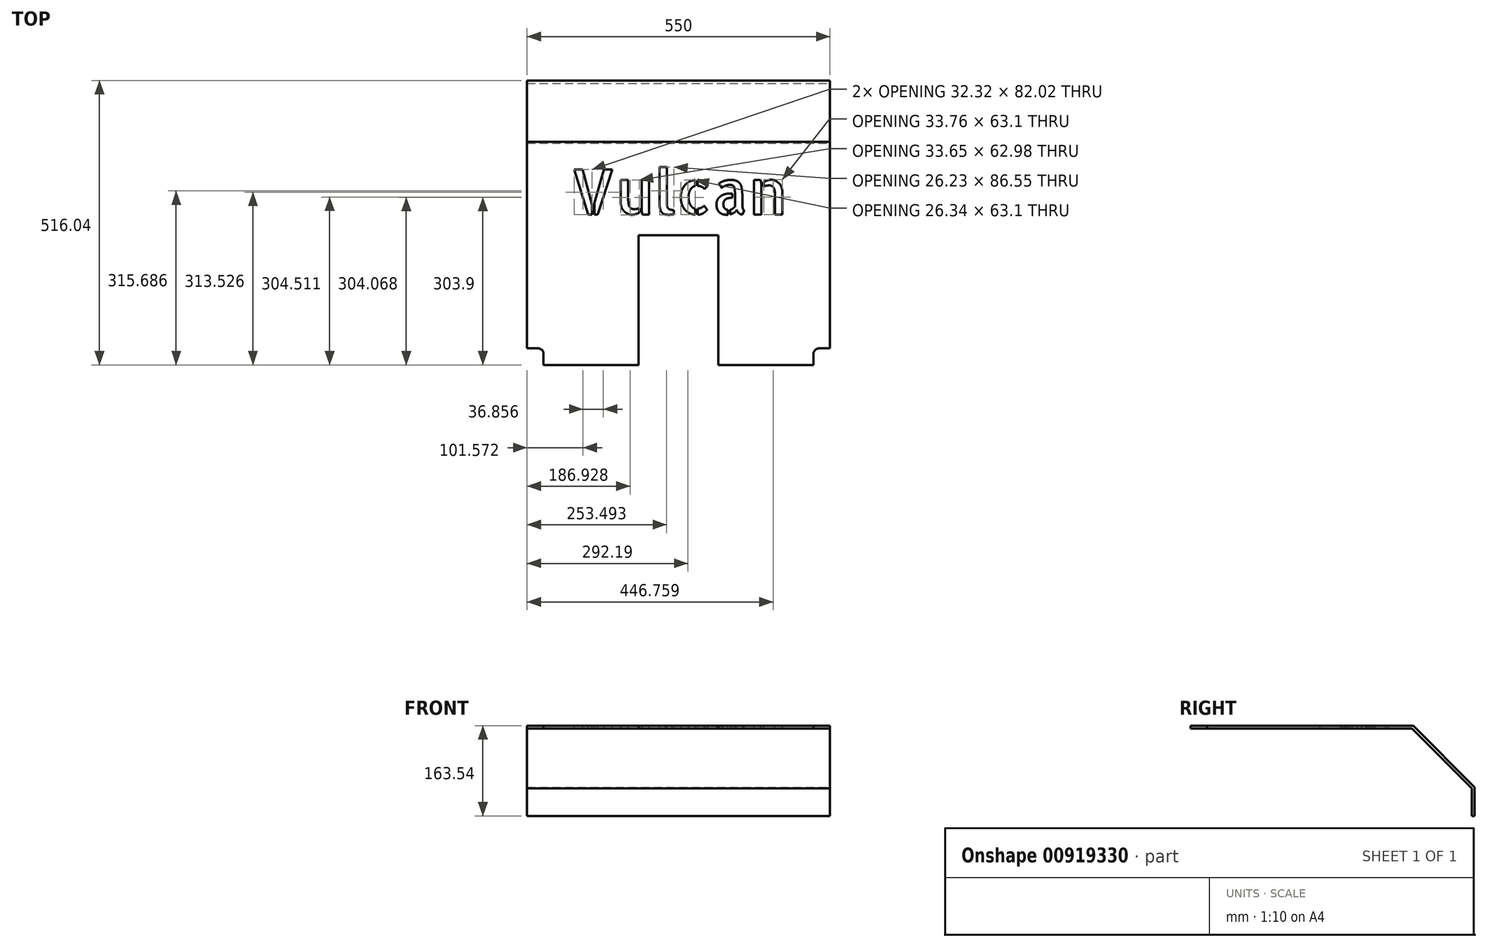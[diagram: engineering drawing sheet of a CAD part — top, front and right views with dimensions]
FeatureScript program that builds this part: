
annotation { "Feature Type Name" : "Feature", "Feature Type Description" : "" }
export const myFeature = defineFeature(function(context is Context, id is Id, definition is map)
    precondition{}
    {
        {
            var Q0;
            Q0=qCreatedBy(makeId("Front.planeOp"),FACE);
            var sketch = newSketch(context, id + "F0", { "sketchPlane" : qUnion([Q0])});
            skLineSegment(sketch, "E0.bottom", {"start": v(0, 0) * mm, "end": v(-550, 0) * mm});
            skLineSegment(sketch, "E0.top", {"start": v(0, 55) * mm, "end": v(-550, 55) * mm});
            skLineSegment(sketch, "E0.left", {"start": v(0, 0) * mm, "end": v(0, 55) * mm});
            skLineSegment(sketch, "E0.right", {"start": v(-550, 0) * mm, "end": v(-550, 55) * mm});
            skSolve(sketch);
        }
        {
            var Q0;
            Q0 = qSketchRegion(id + "F0", true);
            extrude(context, id + "F1", {"entities" : qUnion([Q0]), "depth" : 5 * mm, "offsetDistance" : 25 * mm});
        }
        {
            var Q0;
            Q0=makeQuery(id+"F1.opExtrude","SWEPT_FACE",FACE,{"disambiguationData":[OSD([sQuery(id+"F0.wireOp",EDGE,"E0.left")])]});
            var sketch = newSketch(context, id + "F2", { "sketchPlane" : qUnion([Q0])});
            skLineSegment(sketch, "E1", {"start": v(0, 55) * mm, "end": v(-5, 50) * mm});
            skSolve(sketch);
        }
        {
            var Q0;
            {var subQ0=sQuery(id+"F2.wireOp",EDGE,"E1");Q0=makeQuery(id+"F2.imprint","IMPRINT",FACE,{"disambiguationData":[TD([[makeQuery(id+"F2.imprint","IMPRINT",EDGE,{"derivedFrom":subQ0}),-1.0]])]});}
            extrude(context, id + "F3", {"entities" : qUnion([Q0]), "operationType" : NewBodyOperationType.REMOVE, "endBound" : BoundingType.THROUGH_ALL, "oppositeDirection" : true, "depth" : 25 * mm, "offsetDistance" : 25 * mm});
        }
        {
            var Q0;
            Q0=makeQuery(id+"F3.boolean.opBoolean","COPY",FACE,{"derivedFrom":makeQuery(id+"F3.opExtrude","SWEPT_FACE",FACE,{"disambiguationData":[OSD([sQuery(id+"F2.wireOp",EDGE,"E1")])]})});
            extrude(context, id + "F4", {"entities" : qUnion([Q0]), "operationType" : NewBodyOperationType.ADD, "depth" : 160.56 * mm, "offsetDistance" : 25 * mm});
        }
        {
            var Q0;
            Q0=makeQuery(id+"F4.boolean.opBoolean","MERGE",FACE,{"derivedFrom":[makeQuery(id+"F1.opExtrude","SWEPT_FACE",FACE,{"disambiguationData":[OSD([sQuery(id+"F0.wireOp",EDGE,"E0.left")])]}),makeQuery(id+"F4.opExtrude","SWEPT_FACE",FACE,{"disambiguationData":[OSD([sQuery(id+"F2.wireOp",EDGE,"E1")])]})]});
            var sketch = newSketch(context, id + "F5", { "sketchPlane" : qUnion([Q0])});
            skLineSegment(sketch, "E2", {"start": v(-113.54, 168.54) * mm, "end": v(-113.54, 158.54) * mm});
            skSolve(sketch);
        }
        {
            var Q0;
            {var subQ0=sQuery(id+"F5.wireOp",EDGE,"E2");Q0=makeQuery(id+"F5.imprint","IMPRINT",FACE,{"disambiguationData":[TD([[makeQuery(id+"F5.imprint","IMPRINT",EDGE,{"derivedFrom":subQ0}),-1.0]])]});}
            extrude(context, id + "F6", {"entities" : qUnion([Q0]), "operationType" : NewBodyOperationType.REMOVE, "endBound" : BoundingType.THROUGH_ALL, "oppositeDirection" : true, "depth" : 25 * mm, "offsetDistance" : 25 * mm});
        }
        {
            var Q0;
            Q0=makeQuery(id+"F6.boolean.opBoolean","COPY",FACE,{"derivedFrom":makeQuery(id+"F6.opExtrude","SWEPT_FACE",FACE,{"disambiguationData":[OSD([sQuery(id+"F5.wireOp",EDGE,"E2")])]})});
            extrude(context, id + "F7", {"entities" : qUnion([Q0]), "operationType" : NewBodyOperationType.ADD, "depth" : 402.5 * mm, "offsetDistance" : 25 * mm});
        }
        {
            var Q0;
            Q0=makeQuery(id+"F7.opExtrude","CAP_FACE",FACE,{"disambiguationData":[OSD([sQuery(id+"F5.wireOp",EDGE,"E2")])],"isStart":false});
            var sketch = newSketch(context, id + "F8", { "sketchPlane" : qUnion([Q0])});
            skLineSegment(sketch, "E3", {"start": v(-550, 163.54) * mm, "end": v(0, 163.54) * mm});
            skSolve(sketch);
        }
        {
            var Q0;
            {var subQ0=sQuery(id+"F8.wireOp",EDGE,"E3");Q0=makeQuery(id+"F8.imprint","IMPRINT",FACE,{"disambiguationData":[TD([[makeQuery(id+"F8.imprint","IMPRINT",EDGE,{"derivedFrom":subQ0}),1.0]])]});}
            extrude(context, id + "F9", {"entities" : qUnion([Q0]), "operationType" : NewBodyOperationType.REMOVE, "endBound" : BoundingType.THROUGH_ALL, "oppositeDirection" : true, "depth" : 25 * mm, "offsetDistance" : 25 * mm});
        }
        {
            var Q0;
            Q0=makeQuery(id+"F7.boolean.opBoolean","MERGE",FACE,{"derivedFrom":[makeQuery(id+"F4.boolean.opBoolean","MERGE",FACE,{"derivedFrom":[makeQuery(id+"F1.opExtrude","SWEPT_FACE",FACE,{"disambiguationData":[OSD([sQuery(id+"F0.wireOp",EDGE,"E0.left")])]}),makeQuery(id+"F4.opExtrude","SWEPT_FACE",FACE,{"disambiguationData":[OSD([sQuery(id+"F2.wireOp",EDGE,"E1")])]})]}),makeQuery(id+"F7.opExtrude","SWEPT_FACE",FACE,{"disambiguationData":[OSD([sQuery(id+"F5.wireOp",EDGE,"E2")])]})]});
            var sketch = newSketch(context, id + "F10", { "sketchPlane" : qUnion([Q0])});
            skLineSegment(sketch, "E4", {"start": v(-111.46, 163.54) * mm, "end": v(0, 52.07) * mm});
            skSolve(sketch);
        }
        {
            var Q0;
            {var subQ0=sQuery(id+"F10.wireOp",EDGE,"E4");Q0=makeQuery(id+"F10.imprint","IMPRINT",FACE,{"disambiguationData":[TD([[makeQuery(id+"F10.imprint","IMPRINT",EDGE,{"derivedFrom":subQ0}),1.0]])]});}
            extrude(context, id + "F11", {"entities" : qUnion([Q0]), "operationType" : NewBodyOperationType.REMOVE, "endBound" : BoundingType.THROUGH_ALL, "oppositeDirection" : true, "depth" : 25 * mm, "offsetDistance" : 25 * mm});
        }
        {
            var Q0;
            Q0=makeQuery(id+"F9.boolean.opBoolean","COPY",FACE,{"derivedFrom":makeQuery(id+"F9.opExtrude","SWEPT_FACE",FACE,{"disambiguationData":[OSD([sQuery(id+"F8.wireOp",EDGE,"E3")])]})});
            var sketch = newSketch(context, id + "F12", { "sketchPlane" : qUnion([Q0])});
            skLineSegment(sketch, "E5.bottom", {"start": v(-347.5, -516.04) * mm, "end": v(-202.5, -516.04) * mm});
            skLineSegment(sketch, "E5.top", {"start": v(-347.5, -281.04) * mm, "end": v(-202.5, -281.04) * mm});
            skLineSegment(sketch, "E5.left", {"start": v(-347.5, -516.04) * mm, "end": v(-347.5, -281.04) * mm});
            skLineSegment(sketch, "E5.right", {"start": v(-202.5, -516.04) * mm, "end": v(-202.5, -281.04) * mm});
            skLineSegment(sketch, "E6.bottom", {"start": v(-550, -516.04) * mm, "end": v(-520, -516.04) * mm});
            skLineSegment(sketch, "E6.top", {"start": v(-550, -486.04) * mm, "end": v(-520, -486.04) * mm});
            skLineSegment(sketch, "E6.left", {"start": v(-550, -516.04) * mm, "end": v(-550, -486.04) * mm});
            skLineSegment(sketch, "E6.right", {"start": v(-520, -516.04) * mm, "end": v(-520, -486.04) * mm});
            skLineSegment(sketch, "E7.bottom", {"start": v(0, -516.04) * mm, "end": v(-30, -516.04) * mm});
            skLineSegment(sketch, "E7.top", {"start": v(0, -486.04) * mm, "end": v(-30, -486.04) * mm});
            skLineSegment(sketch, "E7.left", {"start": v(0, -516.04) * mm, "end": v(0, -486.04) * mm});
            skLineSegment(sketch, "E7.right", {"start": v(-30, -516.04) * mm, "end": v(-30, -486.04) * mm});
            skSolve(sketch);
        }
        {
            var Q0;
            Q0 = qSketchRegion(id + "F12", true);
            extrude(context, id + "F13", {"entities" : qUnion([Q0]), "operationType" : NewBodyOperationType.REMOVE, "endBound" : BoundingType.THROUGH_ALL, "oppositeDirection" : true, "depth" : 25 * mm, "offsetDistance" : 25 * mm});
        }
        {
            var Q0;
            Q0=makeQuery(id+"F13.boolean.opBoolean","COPY",EDGE,{"derivedFrom":makeQuery(id+"F13.opExtrude","SWEPT_EDGE",EDGE,{"disambiguationData":[OSD([sQuery(id+"F12.wireOp",EDGE,"E6.top"),sQuery(id+"F12.wireOp",EDGE,"E6.right")])]})});
            var Q1;
            Q1=makeQuery(id+"F13.boolean.opBoolean","COPY",EDGE,{"derivedFrom":makeQuery(id+"F13.opExtrude","SWEPT_EDGE",EDGE,{"disambiguationData":[OSD([sQuery(id+"F12.wireOp",EDGE,"E7.top"),sQuery(id+"F12.wireOp",EDGE,"E7.right")])]})});
            fillet(context, id + "F14", {"entities" : qUnion([Q0, Q1]), "radius" : 10 * mm, "tangentPropagation" : true, "allowEdgeOverflow" : false});
        }
        {
            var Q0;
            Q0=makeQuery(id+"F9.boolean.opBoolean","COPY",FACE,{"derivedFrom":makeQuery(id+"F9.opExtrude","SWEPT_FACE",FACE,{"disambiguationData":[OSD([sQuery(id+"F8.wireOp",EDGE,"E3")])]})});
            var sketch = newSketch(context, id + "F15", { "sketchPlane" : qUnion([Q0])});
            skText(sketch, "E8", { "text": "Vulcan", "fontName": "AllertaStencil-Regular.ttf"});
            const initialGuessF15  = {"E8": [-0.47123, -0.24308, 1, 0, 0.08161]};
            skSetInitialGuess(sketch, initialGuessF15);
            skSolve(sketch);
        }
        {
            var Q0;
            Q0 = qSketchRegion(id + "F15", true);
            extrude(context, id + "F16", {"entities" : qUnion([Q0]), "operationType" : NewBodyOperationType.REMOVE, "endBound" : BoundingType.THROUGH_ALL, "oppositeDirection" : true, "depth" : 1 * mm, "offsetDistance" : 25 * mm});
        }
    });
